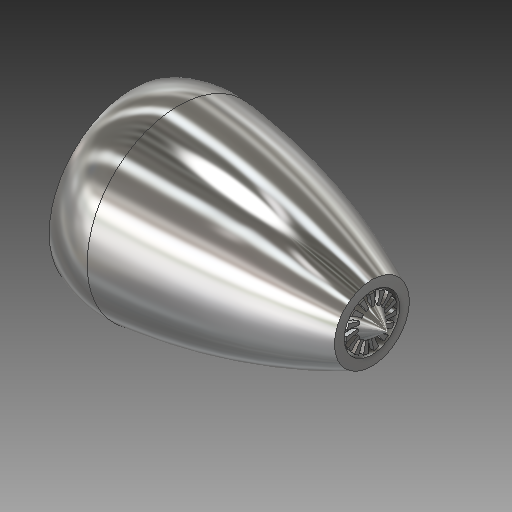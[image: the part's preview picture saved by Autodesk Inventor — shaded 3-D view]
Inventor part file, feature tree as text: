
AUTODESK INVENTOR PART (.ipt)
format: ipt  version: 2018 (Build 220112000, 112)  size: 629,760 bytes
history: native  units: in
note: dims shown in document units (in); Inventor stores cm internally (conversion verified against a paired STEP export)
features: sketch x18, plane x5, other x3
ambient origin geometry x8: Origin, YZ Plane, XZ Plane, XY Plane, X Axis, Y Axis, Z Axis, Center Point
bodies: Solid1 (feature_tree)
feature tree (26):
  other  "JETENGINE.ipt"
  other  "Solid1::JETENGINE.ipt"
  other  "TaggingFeature1"
  sketch  "Sketch1"  dims[d0=0.3937in]
  sketch  "Sketch2"
  sketch  "Sketch3"
  sketch  "Sketch4"
  sketch  "Sketch5"
  sketch  "Sketch6"
  sketch  "Sketch7"
  sketch  "Sketch8"
  sketch  "Sketch9"
  sketch  "Sketch10"
  sketch  "Sketch11"
  sketch  "Sketch12"
  sketch  "Sketch13"
  sketch  "Sketch14"
  sketch  "Sketch15"
  sketch  "Sketch16"
  sketch  "Sketch17"
  sketch  "Sketch18"
  plane  "Work Plane1"
  plane  "Work Plane2"
  plane  "Work Plane3"
  plane  "Work Plane4"
  plane  "Work Plane5"
